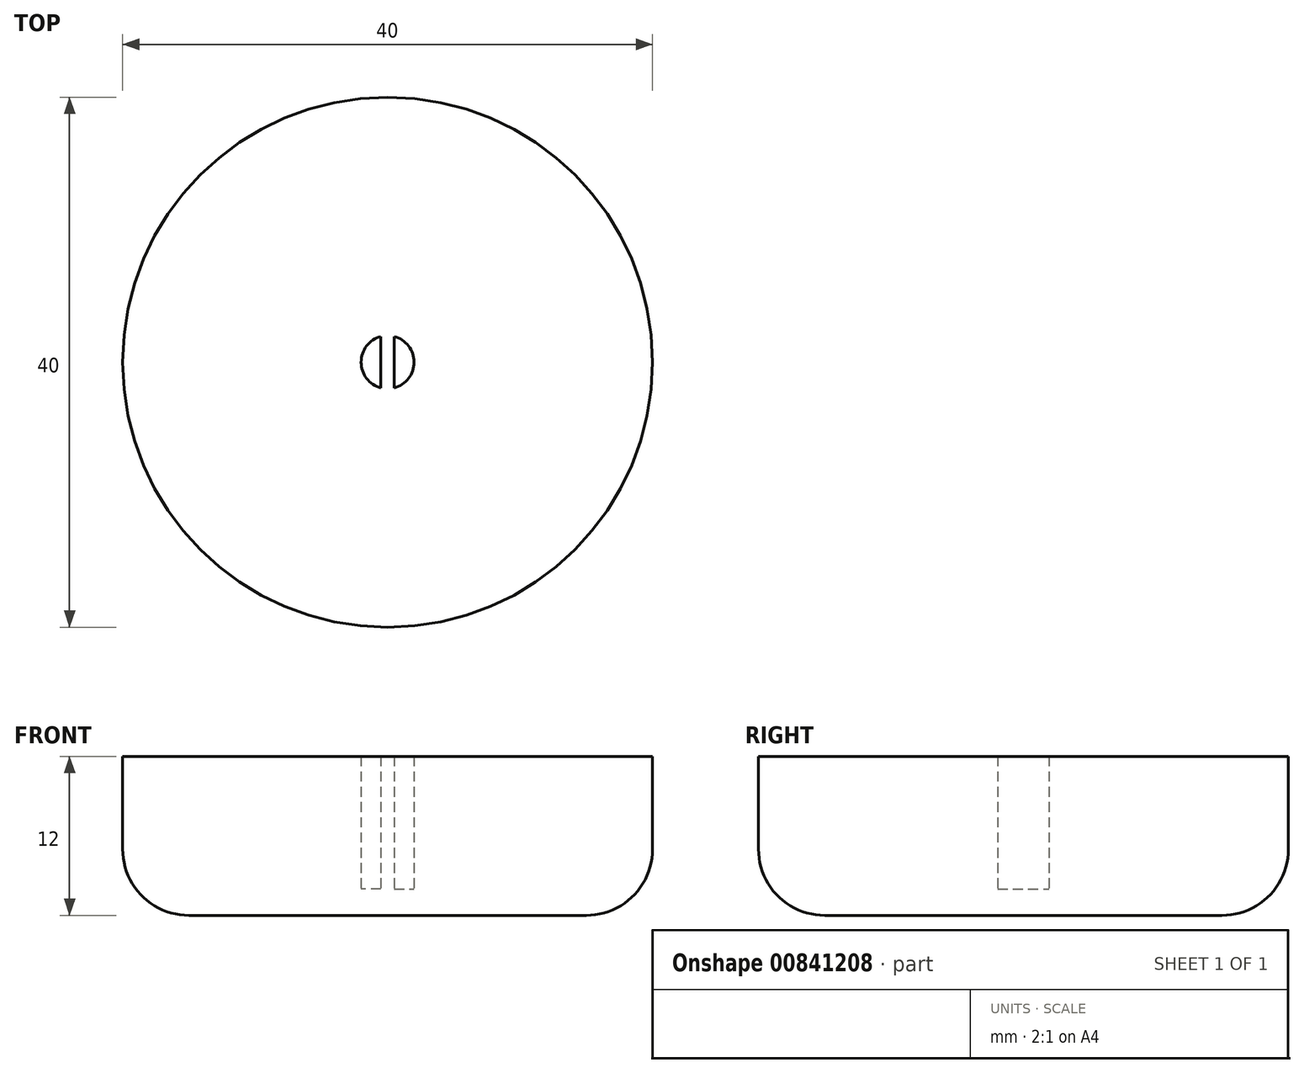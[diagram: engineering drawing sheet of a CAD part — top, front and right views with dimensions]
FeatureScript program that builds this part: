
annotation { "Feature Type Name" : "Feature", "Feature Type Description" : "" }
export const myFeature = defineFeature(function(context is Context, id is Id, definition is map)
    precondition{}
    {
        {
            var Q0;
            Q0=qCreatedBy(makeId("Top.planeOp"),FACE);
            var sketch = newSketch(context, id + "F0", { "sketchPlane" : qUnion([Q0])});
            skCircle(sketch, "E0", {"center": v(0, 0) * mm, "radius": 2 * mm});
            skLineSegment(sketch, "E1", {"start": v(0, 0) * mm, "end": v(-0.5, 0) * mm});
            skLineSegment(sketch, "E2", {"start": v(-0.5, 0) * mm, "end": v(-0.5, 1.94) * mm});
            skLineSegment(sketch, "E3.MirrorCS", {"start": v(-0.5, 0) * mm, "end": v(-0.5, -1.94) * mm});
            skLineSegment(sketch, "E4.MirrorCS", {"start": v(0.5, 0) * mm, "end": v(0.5, 1.94) * mm});
            skLineSegment(sketch, "E5.MirrorCS", {"start": v(0.5, 0) * mm, "end": v(0.5, -1.94) * mm});
            skCircle(sketch, "E6", {"center": v(0, 0) * mm, "radius": 20 * mm});
            skSolve(sketch);
        }
        {
            var Q0;
            Q0=makeQuery(id+"F0.imprint","IMPRINT",FACE,{"disambiguationData":[TD([[makeQuery(id+"F0.imprint","IMPRINT",EDGE,{"derivedFrom":sQuery(id+"F0.wireOp",EDGE,"E6")}),1.0]])]});
            var Q1;
            {var subQ0=sQuery(id+"F0.wireOp",EDGE,"E2");Q1=makeQuery(id+"F0.imprint","IMPRINT",FACE,{"disambiguationData":[TD([[makeQuery(id+"F0.imprint","IMPRINT",EDGE,{"derivedFrom":subQ0}),-1.0]])]});}
            extrude(context, id + "F1", {"entities" : qUnion([Q0, Q1]), "depth" : 10 * mm, "offsetDistance" : 25 * mm});
        }
        {
            var Q0;
            Q0=makeQuery(id+"F0.imprint","IMPRINT",FACE,{"disambiguationData":[TD([[makeQuery(id+"F0.imprint","IMPRINT",EDGE,{"derivedFrom":sQuery(id+"F0.wireOp",EDGE,"E6")}),1.0]])]});
            var Q1;
            {var subQ0=sQuery(id+"F0.wireOp",EDGE,"E4.MirrorCS");Q1=makeQuery(id+"F0.imprint","IMPRINT",FACE,{"disambiguationData":[TD([[makeQuery(id+"F0.imprint","IMPRINT",EDGE,{"derivedFrom":subQ0}),-1.0]])]});}
            var Q2;
            {var subQ0=sQuery(id+"F0.wireOp",EDGE,"E2");Q2=makeQuery(id+"F0.imprint","IMPRINT",FACE,{"disambiguationData":[TD([[makeQuery(id+"F0.imprint","IMPRINT",EDGE,{"derivedFrom":subQ0}),1.0]])]});}
            var Q3;
            {var subQ0=sQuery(id+"F0.wireOp",EDGE,"E2");Q3=makeQuery(id+"F0.imprint","IMPRINT",FACE,{"disambiguationData":[TD([[makeQuery(id+"F0.imprint","IMPRINT",EDGE,{"derivedFrom":subQ0}),-1.0]])]});}
            extrude(context, id + "F2", {"entities" : qUnion([Q0, Q1, Q2, Q3]), "operationType" : NewBodyOperationType.ADD, "oppositeDirection" : true, "depth" : 2 * mm, "offsetDistance" : 25 * mm});
        }
        {
            var Q0;
            Q0=makeQuery(id+"F2.opExtrude","CAP_EDGE",EDGE,{"disambiguationData":[OSD([sQuery(id+"F0.wireOp",EDGE,"E6")])],"isStart":false});
            fillet(context, id + "F3", {"entities" : qUnion([Q0]), "radius" : 5 * mm, "tangentPropagation" : true, "allowEdgeOverflow" : false});
        }
    });
